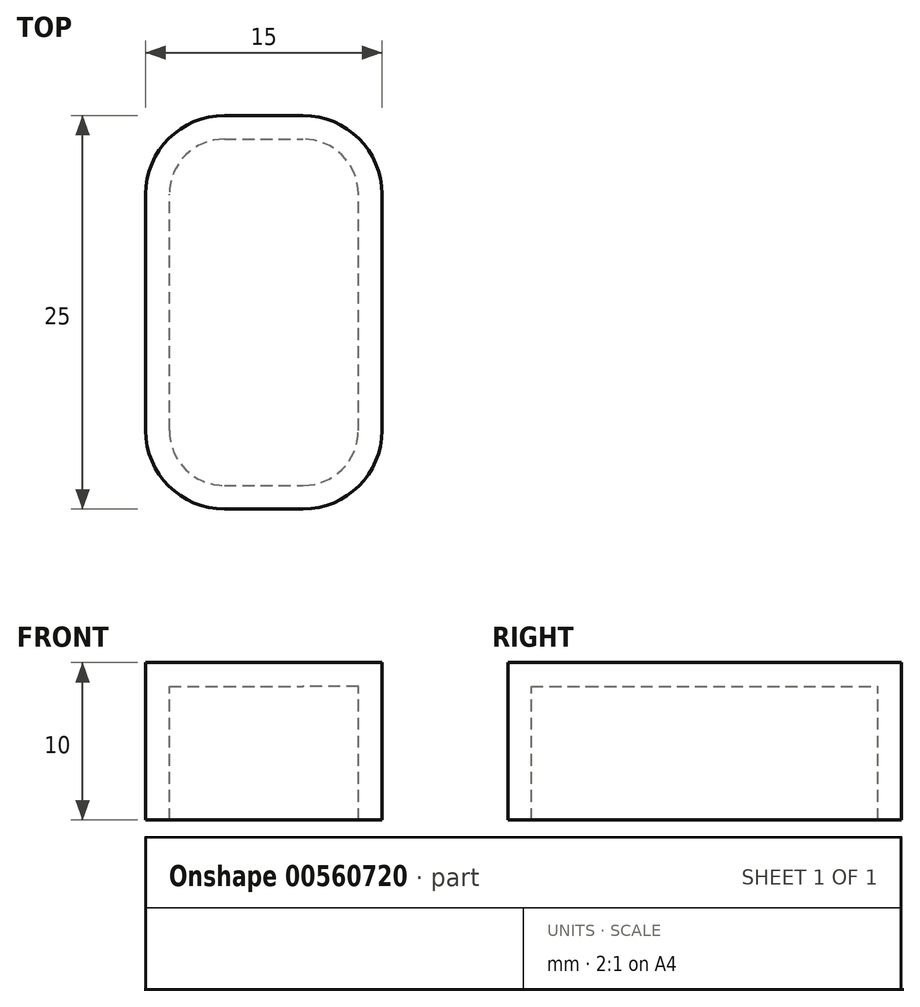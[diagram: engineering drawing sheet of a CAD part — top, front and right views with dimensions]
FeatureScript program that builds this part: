
annotation { "Feature Type Name" : "Feature", "Feature Type Description" : "" }
export const myFeature = defineFeature(function(context is Context, id is Id, definition is map)
    precondition{}
    {
        {
            var Q0;
            Q0=qCreatedBy(makeId("Top.planeOp"),FACE);
            var sketch = newSketch(context, id + "F0", { "sketchPlane" : qUnion([Q0])});
            skLineSegment(sketch, "E0.bottom", {"start": v(-1.8, 6.6) * mm, "end": v(13.2, 6.6) * mm});
            skLineSegment(sketch, "E0.top", {"start": v(-1.8, 31.6) * mm, "end": v(13.2, 31.6) * mm});
            skLineSegment(sketch, "E0.left", {"start": v(-1.8, 6.6) * mm, "end": v(-1.8, 31.6) * mm});
            skLineSegment(sketch, "E0.right", {"start": v(13.2, 6.6) * mm, "end": v(13.2, 31.6) * mm});
            skSolve(sketch);
        }
        {
            var Q0;
            Q0 = qSketchRegion(id + "F0", true);
            extrude(context, id + "F1", {"entities" : qUnion([Q0]), "depth" : 10 * mm, "offsetDistance" : 25 * mm});
        }
        {
            var Q0;
            Q0=makeQuery(id+"F1.opExtrude","SWEPT_EDGE",EDGE,{"disambiguationData":[OSD([sQuery(id+"F0.wireOp",EDGE,"E0.bottom"),sQuery(id+"F0.wireOp",EDGE,"E0.right")])]});
            var Q1;
            Q1=makeQuery(id+"F1.opExtrude","SWEPT_EDGE",EDGE,{"disambiguationData":[OSD([sQuery(id+"F0.wireOp",EDGE,"E0.bottom"),sQuery(id+"F0.wireOp",EDGE,"E0.left")])]});
            var Q2;
            Q2=makeQuery(id+"F1.opExtrude","SWEPT_EDGE",EDGE,{"disambiguationData":[OSD([sQuery(id+"F0.wireOp",EDGE,"E0.top"),sQuery(id+"F0.wireOp",EDGE,"E0.right")])]});
            var Q3;
            Q3=makeQuery(id+"F1.opExtrude","SWEPT_EDGE",EDGE,{"disambiguationData":[OSD([sQuery(id+"F0.wireOp",EDGE,"E0.top"),sQuery(id+"F0.wireOp",EDGE,"E0.left")])]});
            fillet(context, id + "F2", {"entities" : qUnion([Q0, Q1, Q2, Q3]), "radius" : 5 * mm, "tangentPropagation" : true, "allowEdgeOverflow" : false});
        }
        {
            var Q0;
            Q0=makeQuery(id+"F1.opExtrude","CAP_FACE",FACE,{"disambiguationData":[OSD([sQuery(id+"F0.wireOp",EDGE,"E0.bottom"),sQuery(id+"F0.wireOp",EDGE,"E0.top"),sQuery(id+"F0.wireOp",EDGE,"E0.left"),sQuery(id+"F0.wireOp",EDGE,"E0.right")])],"isStart":true});
            shell(context, id + "F3", {"entities" : qUnion([Q0]), "thickness" : 1.5 * mm});
        }
    });
